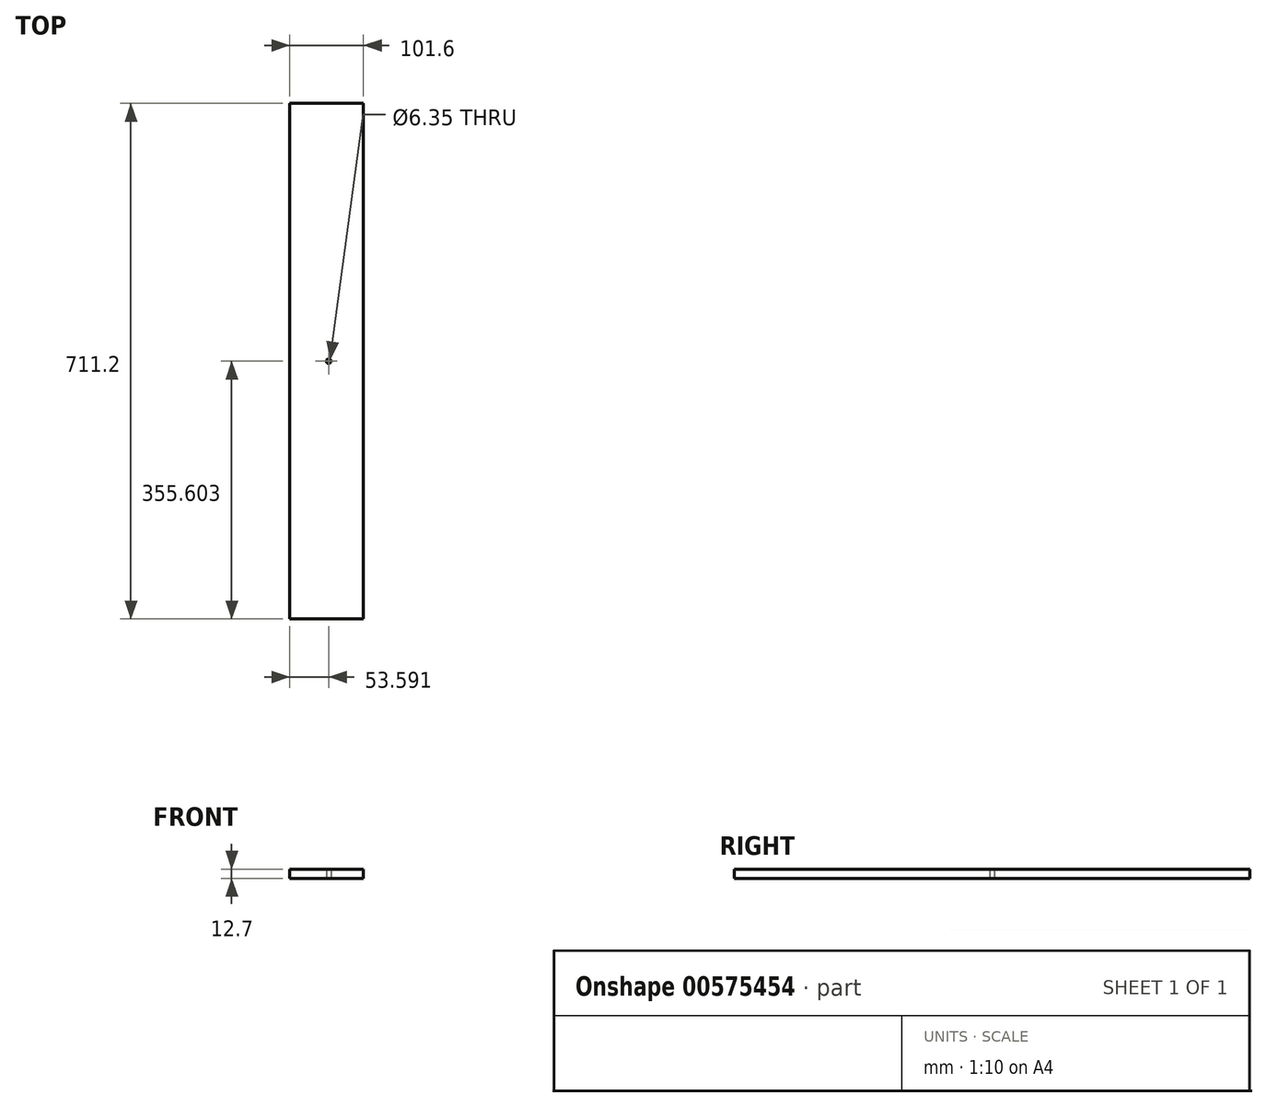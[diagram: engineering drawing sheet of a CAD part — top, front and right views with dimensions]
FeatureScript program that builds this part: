
annotation { "Feature Type Name" : "Feature", "Feature Type Description" : "" }
export const myFeature = defineFeature(function(context is Context, id is Id, definition is map)
    precondition{}
    {
        {
            var Q0;
            Q0=qCreatedBy(makeId("Top.planeOp"),FACE);
            var sketch = newSketch(context, id + "F0", { "sketchPlane" : qUnion([Q0])});
            skLineSegment(sketch, "E0.bottom", {"start": v(-79.2, -195.28) * mm, "end": v(22.4, -195.28) * mm});
            skLineSegment(sketch, "E0.top", {"start": v(-79.2, 515.92) * mm, "end": v(22.4, 515.92) * mm});
            skLineSegment(sketch, "E0.left", {"start": v(-79.2, -195.28) * mm, "end": v(-79.2, 515.92) * mm});
            skLineSegment(sketch, "E0.right", {"start": v(22.4, -195.28) * mm, "end": v(22.4, 515.92) * mm});
            skCircle(sketch, "E1", {"center": v(-25.6, 160.32) * mm, "radius": 3.18 * mm});
            skPoint(sketch, "E1.centerSnap0", {"position": v(22.4, 160.32) * mm});
            skSolve(sketch);
        }
        {
            var Q0;
            Q0=makeQuery(id+"F0.imprint","IMPRINT",FACE,{"disambiguationData":[TD([[makeQuery(id+"F0.imprint","IMPRINT",EDGE,{"derivedFrom":sQuery(id+"F0.wireOp",EDGE,"E0.bottom")}),1.0]])]});
            extrude(context, id + "F1", {"entities" : qUnion([Q0]), "depth" : 12.7 * mm, "offsetDistance" : 25.4 * mm});
        }
    });
